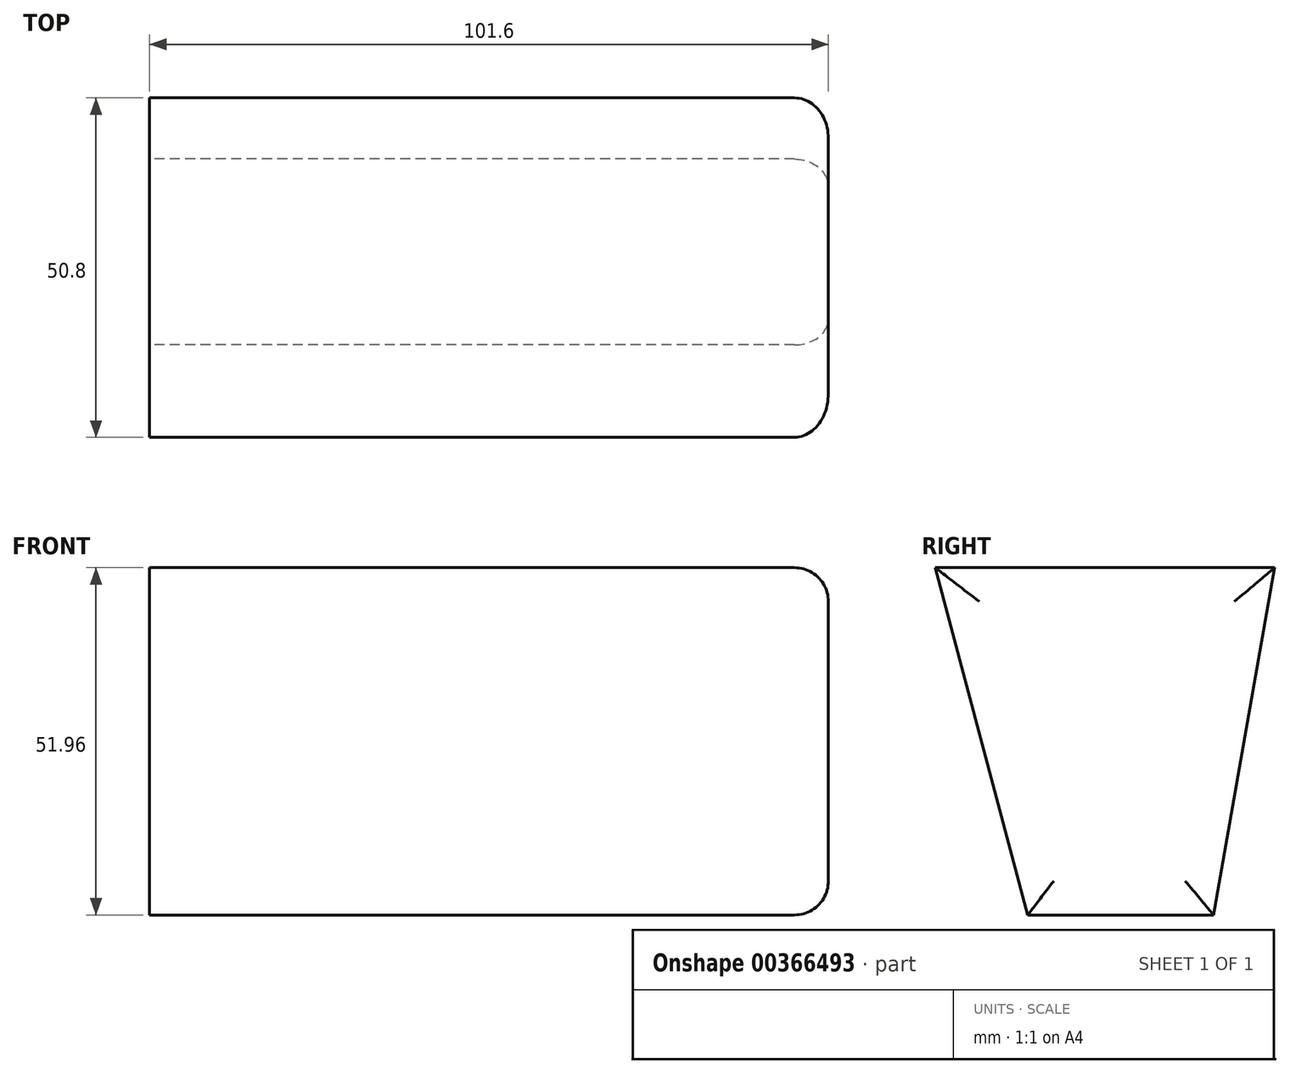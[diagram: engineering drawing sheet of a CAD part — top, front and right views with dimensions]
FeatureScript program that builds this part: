
annotation { "Feature Type Name" : "Feature", "Feature Type Description" : "" }
export const myFeature = defineFeature(function(context is Context, id is Id, definition is map)
    precondition{}
    {
        {
            var Q0;
            Q0=qCreatedBy(makeId("Right.planeOp"),FACE);
            var sketch = newSketch(context, id + "F0", { "sketchPlane" : qUnion([Q0])});
            skLineSegment(sketch, "E0.bottom", {"start": v(-23.1, 46.32) * mm, "end": v(27.7, 46.32) * mm});
            skLineSegment(sketch, "E0.top", {"start": v(-23.1, -29.88) * mm, "end": v(27.7, -29.88) * mm});
            skLineSegment(sketch, "E0.left", {"start": v(-23.1, 46.32) * mm, "end": v(-23.1, -29.88) * mm});
            skLineSegment(sketch, "E0.right", {"start": v(27.7, 46.32) * mm, "end": v(27.7, -29.88) * mm});
            skLineSegment(sketch, "E1", {"start": v(27.7, 46.32) * mm, "end": v(18.54, -5.64) * mm});
            skLineSegment(sketch, "E2", {"start": v(-9.27, -5.64) * mm, "end": v(-23.1, 46.32) * mm});
            skLineSegment(sketch, "E3", {"start": v(-9.27, -5.64) * mm, "end": v(18.54, -5.64) * mm});
            skSolve(sketch);
        }
        {
            var Q0;
            Q0=makeQuery(id+"F0.imprint","IMPRINT",FACE,{"disambiguationData":[TD([[makeQuery(id+"F0.imprint","IMPRINT",EDGE,{"derivedFrom":sQuery(id+"F0.wireOp",EDGE,"E0.bottom")}),-1.0]])]});
            extrude(context, id + "F1", {"entities" : qUnion([Q0]), "depth" : 101.6 * mm});
        }
        {
            var Q0;
            Q0=makeQuery(id+"F1.opExtrude","CAP_FACE",FACE,{"disambiguationData":[OSD([sQuery(id+"F0.wireOp",EDGE,"E0.bottom"),sQuery(id+"F0.wireOp",EDGE,"E0.top"),sQuery(id+"F0.wireOp",EDGE,"E0.left"),sQuery(id+"F0.wireOp",EDGE,"E0.right")])],"isStart":false});
            fillet(context, id + "F2", {"entities" : qUnion([Q0]), "radius" : 5.08 * mm, "tangentPropagation" : true, "allowEdgeOverflow" : false});
        }
    });
